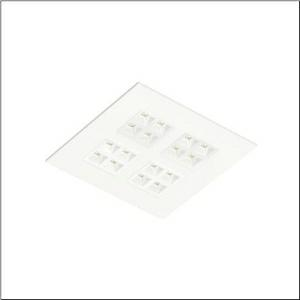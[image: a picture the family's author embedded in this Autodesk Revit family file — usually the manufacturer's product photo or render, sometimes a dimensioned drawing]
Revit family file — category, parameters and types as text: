
# Revit family: silica_31_square_51my6nmu34wa
name_source: partatom
category: Lighting Fixtures
units: mm (PartAtom-declared; Revit-internal decimal feet)

## family parameters
Cut with Voids When Loaded = No
Host = Face
Light Source = No
Part Type = Normal
Room Calculation Point = No
Round Connector Dimension = Use Diameter
Shared = No

## types (1)
- --- (1 x LED, 6600 lm, 39 W, 3000K)
    Apparent Load = 39 VA
    CIE Flux Codes = 81 99 100 100 100
    Color Rendering = 80
    Color Temperature = 3000K
    Default Elevation = 1800 mm
    Description = Silica 31 Square, office luminaire, primary light control with lens, of PMMA, primary anti-glare with reflector, of PC, white, light emission: direct distribution, primary light characteristic: symmetric, installation type: lay-in mounting, LED, rated luminous flux: 4.580lm, luminous efficacy: 176lm/W, light colour: 830, colour temperature: 3000K, control gear: ON/OFF Multilumen, with terminal, 3-pole, mains connection: 220..240V, AC, 50/60Hz, rated input power: 26W, luminaire housing, of sheet steel, coated, traffic white (RAL 9016), module: M625, length: 620mm, width: 620mm, height: 43mm, protection rating (complete): IP20, insulation class (complete): insulation class II (safety insulation), certification: CE, impact resistance: IK03, permissible operating ambient temperature: -20..+35°C, standard: EN 50419, packaging unit: 1 piece
    Height = 0 mm  [stored 0 ft]
    Lamp = 1 x LED
    Lamp Light Flux = 6600 lm
    Lamp Power = 39 W
    Lamp count = 1
    Length = 620 mm
    Luminous efficacy = 169 lm/W
    Manufacturer = Siteco
    ModVariant = No
    Model = 51MY6NMU34WA
    Mounting Place = Ceiling
    Mounting Type = Recessed
    Number of Poles = 1
    OnlyDefault = Yes
    Power Factor = 1
    Product Name = Silica 31 Square
    Product group = office luminaire | ceiling recessed
    ProductGroupID = 400
    Protection Class = Protection class II
    Protection Degree = IP 20
    RLX_Detail_Level = 1
    RLX_Emergency_Light_Flux = 0 lm
    RLX_Emergency_Type = 0
    RLX_Emergency_Type_DB = No
    RlxData = <blob elided: 28525 chars, md5=6574e9a7>
    Socket = socket
    Standby Power = 0 W
    System Light Flux = 6600 lm
    System Power = 39 W
    Type Comments = factory setting: luminous flux: 100 % | (ON | ON | ON | ON) | 1100 mA
    Type Image = l_1313651.jpg
    URL = http://relux.com
    VarID = @adj_043111
    Voltage = 0 V
    Weight = 0.00 kg
    Width = 620 mm

note: [stored X ft] marks values corroborated as IEEE doubles in the binary element streams (Revit-internal decimal feet)

## geometry (parser evidence)
native form markers: Blend x4, Sweep x9
no freeform markers — native parametric forms only
